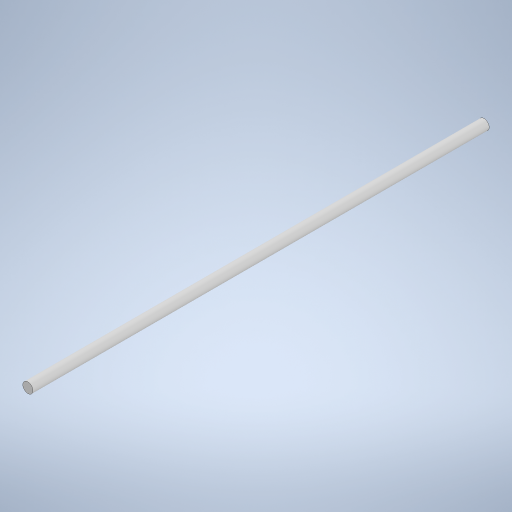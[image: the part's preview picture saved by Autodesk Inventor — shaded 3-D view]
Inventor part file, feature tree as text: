
AUTODESK INVENTOR PART (.ipt)
format: ipt  version: 2024 (Build 280153000, 153)  size: 235,008 bytes
history: native  units: mm
features: extrude x1, sketch x1
ambient origin geometry x8: Origin, YZ Plane, XZ Plane, XY Plane, X Axis, Y Axis, Z Axis, Center Point
bodies: Solid1 (feature_tree)
feature tree (2):
  extrude  "Extrusion1"  Depth=90.0mm TaperAngle=0.0deg
  sketch  "Sketch1"  dims[d0=2.0mm d1=90.0mm d2=0.0mm]
